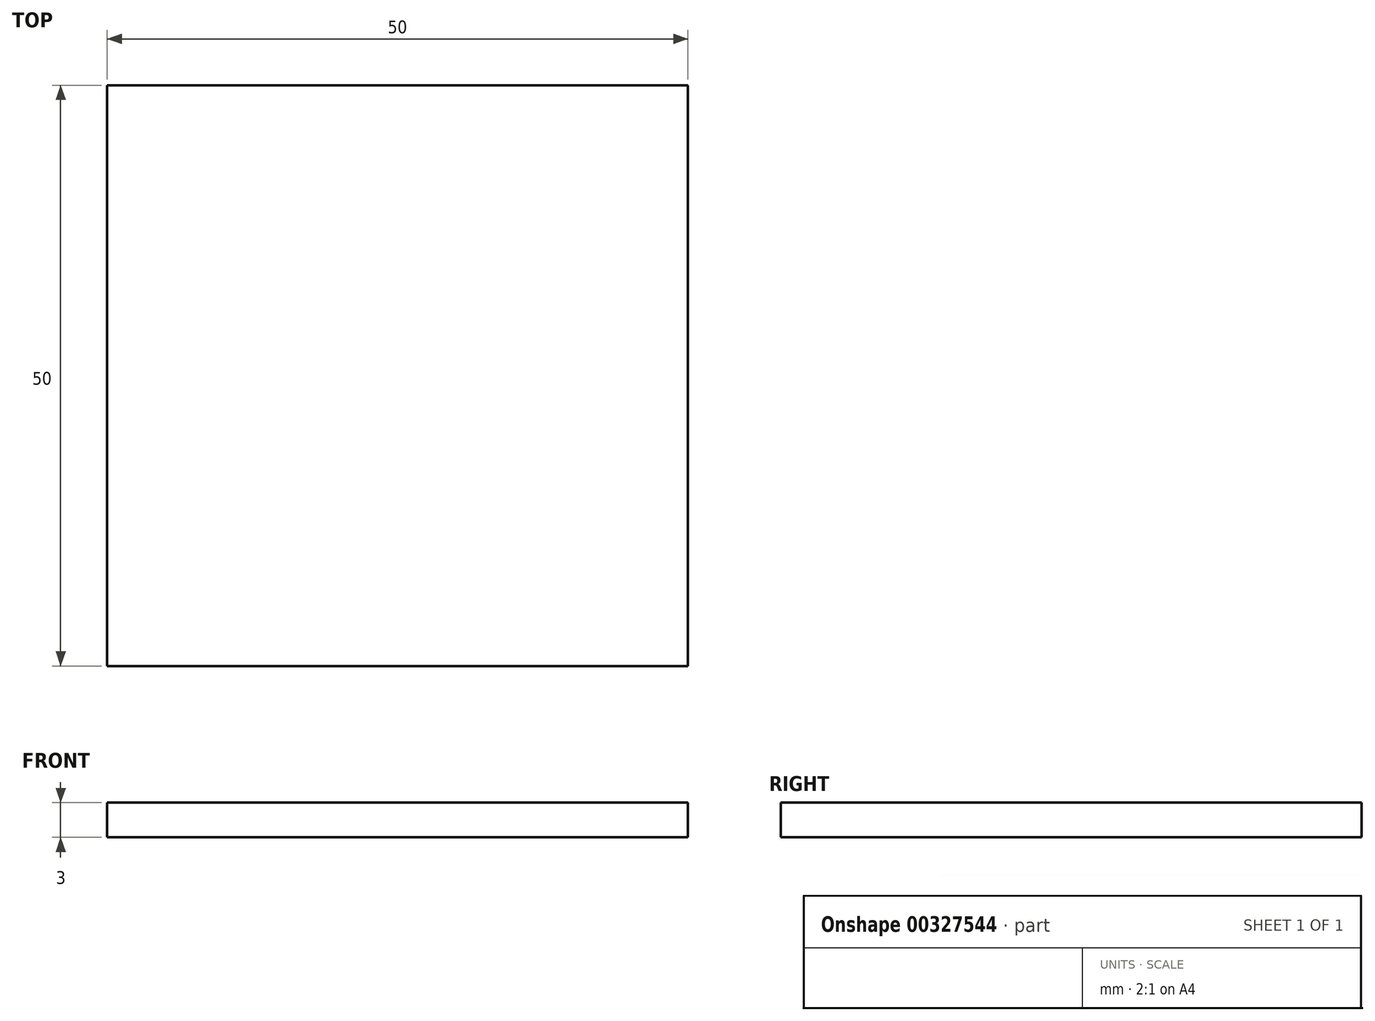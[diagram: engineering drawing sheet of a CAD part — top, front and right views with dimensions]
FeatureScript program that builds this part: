
annotation { "Feature Type Name" : "Feature", "Feature Type Description" : "" }
export const myFeature = defineFeature(function(context is Context, id is Id, definition is map)
    precondition{}
    {
        {
            var Q0;
            Q0=qCreatedBy(makeId("Top.planeOp"),FACE);
            var sketch = newSketch(context, id + "F0", { "sketchPlane" : qUnion([Q0])});
            skLineSegment(sketch, "E0.bottom", {"start": v(-25, 25) * mm, "end": v(25, 25) * mm});
            skLineSegment(sketch, "E0.top", {"start": v(-25, -25) * mm, "end": v(25, -25) * mm});
            skLineSegment(sketch, "E0.left", {"start": v(-25, 25) * mm, "end": v(-25, -25) * mm});
            skLineSegment(sketch, "E0.right", {"start": v(25, 25) * mm, "end": v(25, -25) * mm});
            skPoint(sketch, "E0.middle", {"position": v(0, 0) * mm});
            skSolve(sketch);
        }
        {
            var Q0;
            Q0 = qSketchRegion(id + "F0", true);
            extrude(context, id + "F1", {"entities" : qUnion([Q0]), "depth" : 3 * mm, "symmetric" : true});
        }
    });
